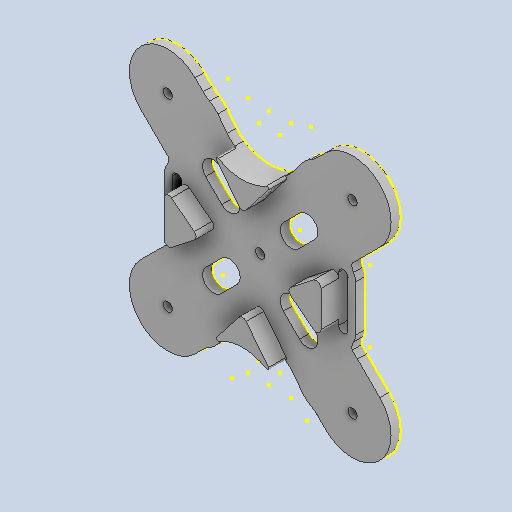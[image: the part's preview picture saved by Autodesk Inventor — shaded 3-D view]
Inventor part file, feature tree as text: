
AUTODESK INVENTOR PART (.ipt)
format: ipt  version: 2023 (Build 270158000, 158)  size: 452,096 bytes
history: native  units: in
note: dims shown in document units (in); Inventor stores cm internally (conversion verified against a paired STEP export)
features: sketch x1, projected_geometry x1, other x1
ambient origin geometry x8: Origin, YZ Plane, XZ Plane, XY Plane, X Axis, Y Axis, Z Axis, Center Point
bodies: Solid2 (feature_tree)
feature tree (3):
  sketch  "Sketch1"
  projected_geometry  "Projected Loop1"
  other  "Body169 (1) (1) (3)"
